# Revit family: DF_ЗажимПараллельный_Пруток_Пруток_8-10_EZETEK
name_source: partatom
category: Соединительные детали воздуховодов
revit_build: Autodesk Revit 2017 (Build: 20170118_1100(x64)
units: mm (PartAtom-declared; Revit-internal decimal feet)

## family parameters
Всегда вертикально = Да
На основе рабочей плоскости = Нет
Общий = Нет
При загрузке вырезать с полостями = Нет
Размер круглого соединителя = Использовать радиус
Тип детали = Соединение

## types (3) — shared parameters
ADSK_Версия Revit = 2017
ADSK_Единица измерения = Неспецифицируемое
ADSK_Завод-изготовитель = Неспецифицируемое
ADSK_Код изделия = Неспецифицируемое
ADSK_Марка = Неспецифицируемое
ADSK_Масса_Текст = Неспецифицируемое
ADSK_Наименование = Неспецифицируемое
ADSK_Обозначение = Неспецифицируемое
URL = https://ezetek.ru
Группа модели = Зажимы
Изготовитель = Ezetek
Описание = Зажим позволяет выполнить соединение в параллельном направлении прутков диаметром 8-10 мм между собой. Зажим стягивается болтами М8.
Угол = 0.00°
zero-valued in all types: ADSK_Количество, ADSK_Масса

## per-type parameters (varying)
| type | ADSK_Материал | Тип |
| ЗажимПараллельный_Стержень-Стержень_Латунь_90553-2 | BIMLIB_Латунь_EZETEK | FA_ЗажимПараллельный_Пруток_Пруток_8-10_EZETEK : ЗажимПараллельный_Пруток_Пруток_Латунь_90553-2 |
| ЗажимПараллельный_Стержень-Стержень_СтальОцинкованная_90550-2 | BIMLIB_Сталь_Оцинкованная_EZETEK | FA_ЗажимПараллельный_Пруток_Пруток_8-10_EZETEK : ЗажимПараллельный_Пруток_Пруток_СтальОцинкованная_90550-2 |
| ЗажимПараллельный_Стержень-Стержень_Медь_90552-2 | BIMLIB_Медь_EZETEK | FA_ЗажимПараллельный_Пруток_Пруток_8-10_EZETEK : ЗажимПараллельный_Пруток_Пруток_Медь_90552-2 |
